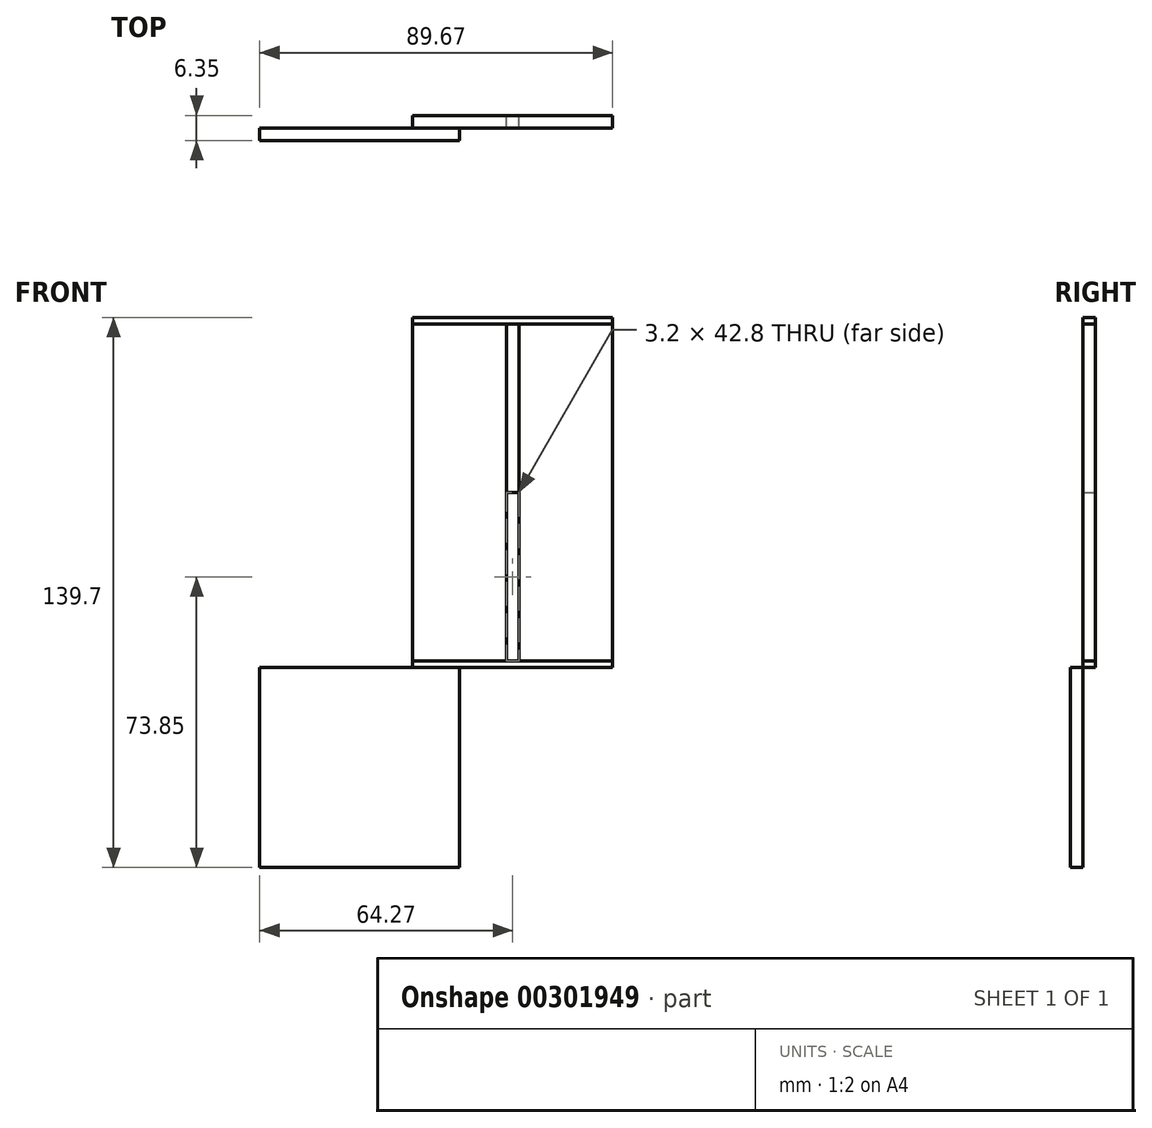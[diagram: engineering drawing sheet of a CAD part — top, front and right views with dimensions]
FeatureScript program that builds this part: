
annotation { "Feature Type Name" : "Feature", "Feature Type Description" : "" }
export const myFeature = defineFeature(function(context is Context, id is Id, definition is map)
    precondition{}
    {
        {
            var Q0;
            Q0=qCreatedBy(makeId("Front.planeOp"),FACE);
            var sketch = newSketch(context, id + "F0", { "sketchPlane" : qUnion([Q0])});
            skLineSegment(sketch, "E0.bottom", {"start": v(25.4, -44.45) * mm, "end": v(-25.4, -44.45) * mm});
            skLineSegment(sketch, "E0.top", {"start": v(25.4, 44.45) * mm, "end": v(-25.4, 44.45) * mm});
            skLineSegment(sketch, "E0.left", {"start": v(25.4, -44.45) * mm, "end": v(25.4, 44.45) * mm});
            skLineSegment(sketch, "E0.right", {"start": v(-25.4, -44.45) * mm, "end": v(-25.4, 44.45) * mm});
            skPoint(sketch, "E0.middle", {"position": v(0, 0) * mm});
            skSolve(sketch);
        }
        {
            var Q0;
            Q0=makeQuery(id+"F0.imprint","IMPRINT",FACE,{"disambiguationData":[TD([[makeQuery(id+"F0.imprint","IMPRINT",EDGE,{"derivedFrom":sQuery(id+"F0.wireOp",EDGE,"E0.bottom")}),-1.0]])]});
            extrude(context, id + "F1", {"entities" : qUnion([Q0]), "depth" : 3.17 * mm});
        }
        {
            var Q0;
            Q0 = qSketchRegion(id + "F0", true);
            extrude(context, id + "F2", {"entities" : qUnion([Q0]), "operationType" : NewBodyOperationType.ADD, "depth" : 3.17 * mm});
        }
        {
            var Q0;
            Q0=makeQuery(id+"F1.opExtrude","CAP_FACE",FACE,{"disambiguationData":[OSD([sQuery(id+"F0.wireOp",EDGE,"E0.bottom"),sQuery(id+"F0.wireOp",EDGE,"E0.top"),sQuery(id+"F0.wireOp",EDGE,"E0.left"),sQuery(id+"F0.wireOp",EDGE,"E0.right")])],"isStart":false});
            var sketch = newSketch(context, id + "F3", { "sketchPlane" : qUnion([Q0])});
            skLineSegment(sketch, "E1.bottom", {"start": v(-13.47, -44.45) * mm, "end": v(-64.27, -44.45) * mm});
            skLineSegment(sketch, "E1.top", {"start": v(-13.47, -95.25) * mm, "end": v(-64.27, -95.25) * mm});
            skLineSegment(sketch, "E1.left", {"start": v(-13.47, -44.45) * mm, "end": v(-13.47, -95.25) * mm});
            skLineSegment(sketch, "E1.right", {"start": v(-64.27, -44.45) * mm, "end": v(-64.27, -95.25) * mm});
            skSolve(sketch);
        }
        {
            var Q0;
            Q0=makeQuery(id+"F3.imprint","IMPRINT",FACE,{"disambiguationData":[TD([[makeQuery(id+"F3.imprint","IMPRINT",EDGE,{"derivedFrom":sQuery(id+"F3.wireOp",EDGE,"E1.top")}),-1.0]])]});
            extrude(context, id + "F4", {"entities" : qUnion([Q0]), "depth" : 3.17 * mm});
        }
        {
            var Q0;
            Q0=qCreatedBy(makeId("Front.planeOp"),FACE);
            var sketch = newSketch(context, id + "F5", { "sketchPlane" : qUnion([Q0])});
            skLineSegment(sketch, "E2.bottom", {"start": v(25.4, -42.8) * mm, "end": v(-25.4, -42.8) * mm});
            skLineSegment(sketch, "E2.top", {"start": v(25.4, 42.8) * mm, "end": v(-25.4, 42.8) * mm});
            skLineSegment(sketch, "E2.left", {"start": v(25.4, -42.8) * mm, "end": v(25.4, 42.8) * mm});
            skLineSegment(sketch, "E2.right", {"start": v(-25.4, -42.8) * mm, "end": v(-25.4, 42.8) * mm});
            skPoint(sketch, "E2.middle", {"position": v(0, 0) * mm});
            skSolve(sketch);
        }
        {
            var Q0;
            Q0 = qSketchRegion(id + "F5", true);
            extrude(context, id + "F6", {"entities" : qUnion([Q0]), "depth" : 3.17 * mm});
        }
        {
            var Q0;
            Q0=makeQuery(id+"F6.opExtrude","CAP_FACE",FACE,{"disambiguationData":[OSD([sQuery(id+"F5.wireOp",EDGE,"E2.bottom"),sQuery(id+"F5.wireOp",EDGE,"E2.top"),sQuery(id+"F5.wireOp",EDGE,"E2.left"),sQuery(id+"F5.wireOp",EDGE,"E2.right")])],"isStart":false});
            var sketch = newSketch(context, id + "F7", { "sketchPlane" : qUnion([Q0])});
            skLineSegment(sketch, "E3.bottom", {"start": v(-1.6, -42.8) * mm, "end": v(1.6, -42.8) * mm});
            skLineSegment(sketch, "E3.top", {"start": v(-1.6, 0) * mm, "end": v(1.6, 0) * mm});
            skLineSegment(sketch, "E3.left", {"start": v(-1.6, -42.8) * mm, "end": v(-1.6, 0) * mm});
            skLineSegment(sketch, "E3.right", {"start": v(1.6, -42.8) * mm, "end": v(1.6, 0) * mm});
            skSolve(sketch);
        }
        {
            var Q0;
            Q0 = qSketchRegion(id + "F7", true);
            extrude(context, id + "F8", {"entities" : qUnion([Q0]), "operationType" : NewBodyOperationType.REMOVE, "oppositeDirection" : true, "depth" : 25.4 * mm});
        }
        {
            var Q0;
            Q0=qCreatedBy(makeId("Front.planeOp"),FACE);
            var sketch = newSketch(context, id + "F9", { "sketchPlane" : qUnion([Q0])});
            skLineSegment(sketch, "E4.bottom", {"start": v(25.4, -42.8) * mm, "end": v(-25.4, -42.8) * mm});
            skLineSegment(sketch, "E4.top", {"start": v(25.4, 42.8) * mm, "end": v(-25.4, 42.8) * mm});
            skLineSegment(sketch, "E4.left", {"start": v(25.4, -42.8) * mm, "end": v(25.4, 42.8) * mm});
            skLineSegment(sketch, "E4.right", {"start": v(-25.4, -42.8) * mm, "end": v(-25.4, 42.8) * mm});
            skPoint(sketch, "E4.middle", {"position": v(0, 0) * mm});
            skLineSegment(sketch, "E5.bottom", {"start": v(-1.6, 42.8) * mm, "end": v(1.6, 42.8) * mm});
            skLineSegment(sketch, "E5.top", {"start": v(-1.6, 0) * mm, "end": v(1.6, 0) * mm});
            skLineSegment(sketch, "E5.left", {"start": v(-1.6, 42.8) * mm, "end": v(-1.6, 0) * mm});
            skLineSegment(sketch, "E5.right", {"start": v(1.6, 42.8) * mm, "end": v(1.6, 0) * mm});
            skSolve(sketch);
        }
        {
            var Q0;
            Q0=makeQuery(id+"F9.imprint","IMPRINT",FACE,{"disambiguationData":[TD([[makeQuery(id+"F9.imprint","IMPRINT",EDGE,{"derivedFrom":sQuery(id+"F9.wireOp",EDGE,"E4.bottom")}),-1.0]])]});
            extrude(context, id + "F10", {"entities" : qUnion([Q0]), "depth" : 3.17 * mm});
        }
    });
